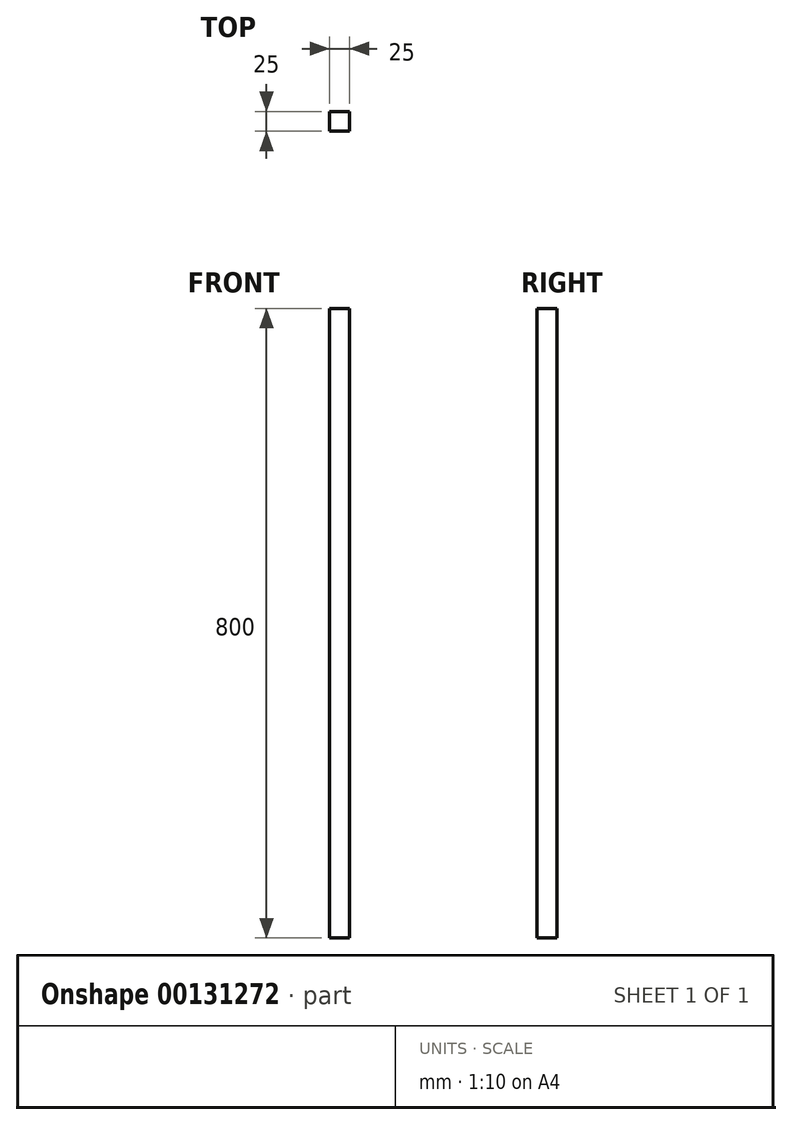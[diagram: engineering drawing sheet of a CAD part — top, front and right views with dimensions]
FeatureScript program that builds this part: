
annotation { "Feature Type Name" : "Feature", "Feature Type Description" : "" }
export const myFeature = defineFeature(function(context is Context, id is Id, definition is map)
    precondition{}
    {
        {
            var Q0;
            Q0=qCreatedBy(makeId("Top.planeOp"),FACE);
            var sketch = newSketch(context, id + "F0", { "sketchPlane" : qUnion([Q0])});
            skLineSegment(sketch, "E0.bottom", {"start": v(-25, 25) * mm, "end": v(0, 25) * mm});
            skLineSegment(sketch, "E0.top", {"start": v(-25, 0) * mm, "end": v(0, 0) * mm});
            skLineSegment(sketch, "E0.left", {"start": v(-25, 25) * mm, "end": v(-25, 0) * mm});
            skLineSegment(sketch, "E0.right", {"start": v(0, 25) * mm, "end": v(0, 0) * mm});
            skSolve(sketch);
        }
        {
            var Q0;
            Q0 = qSketchRegion(id + "F0", true);
            extrude(context, id + "F1", {"entities" : qUnion([Q0]), "depth" : 800 * mm});
        }
    });
